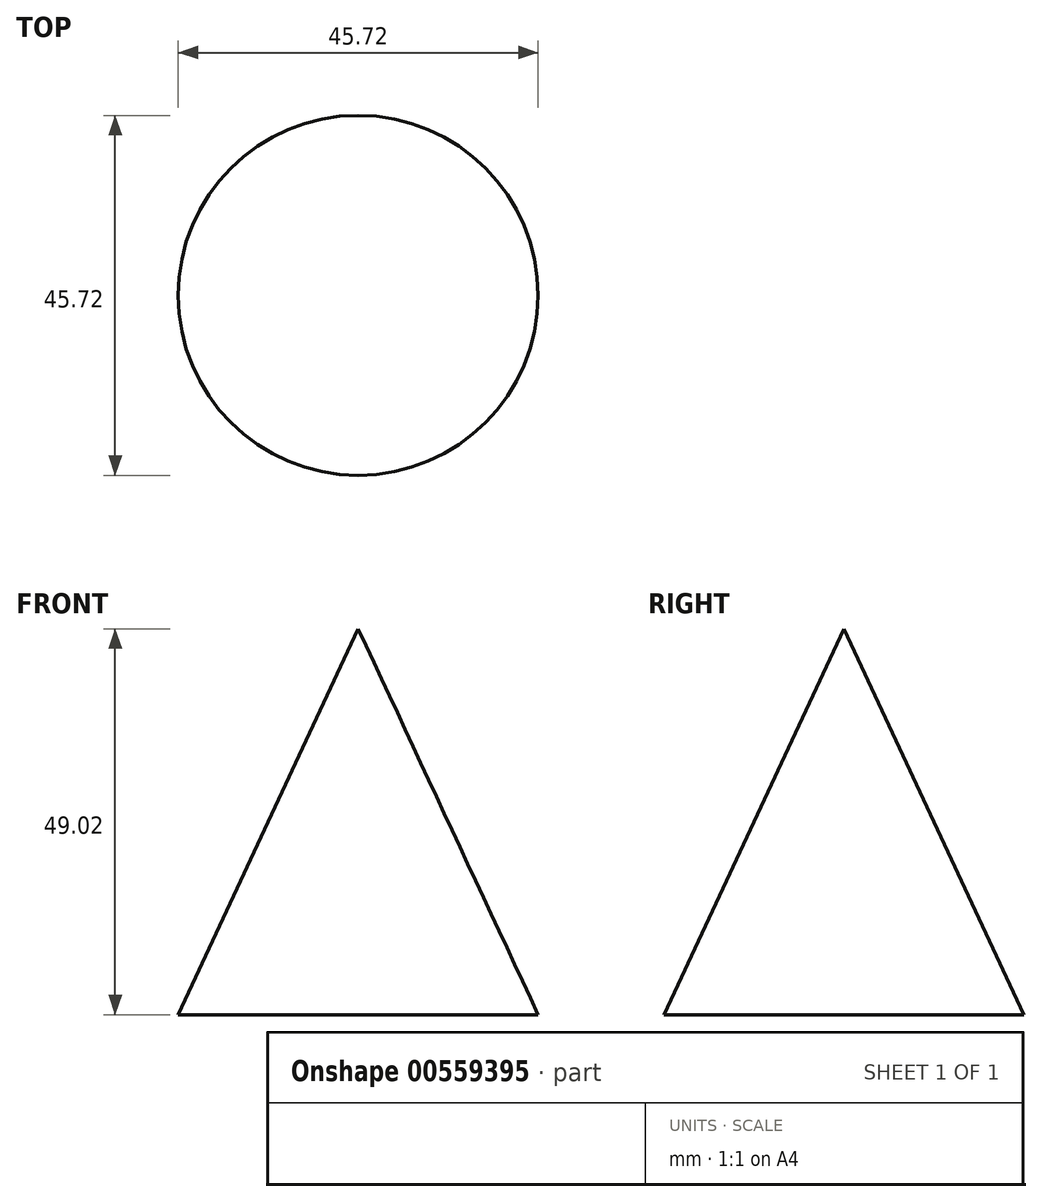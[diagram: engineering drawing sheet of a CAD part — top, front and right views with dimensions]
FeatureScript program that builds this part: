
annotation { "Feature Type Name" : "Feature", "Feature Type Description" : "" }
export const myFeature = defineFeature(function(context is Context, id is Id, definition is map)
    precondition{}
    {
        {
            var Q0;
            Q0=qCreatedBy(makeId("Top.planeOp"),FACE);
            var sketch = newSketch(context, id + "F0", { "sketchPlane" : qUnion([Q0])});
            skCircle(sketch, "E0", {"center": v(0, 0) * mm, "radius": 22.86 * mm});
            skSolve(sketch);
        }
        {
            var Q0;
            Q0 = qSketchRegion(id + "F0", true);
            extrude(context, id + "F1", {"entities" : qUnion([Q0]), "depth" : 50.8 * mm, "offsetDistance" : 25.4 * mm, "hasDraft" : true, "draftAngle" : 25 * degree, "draftPullDirection" : true});
        }
    });
